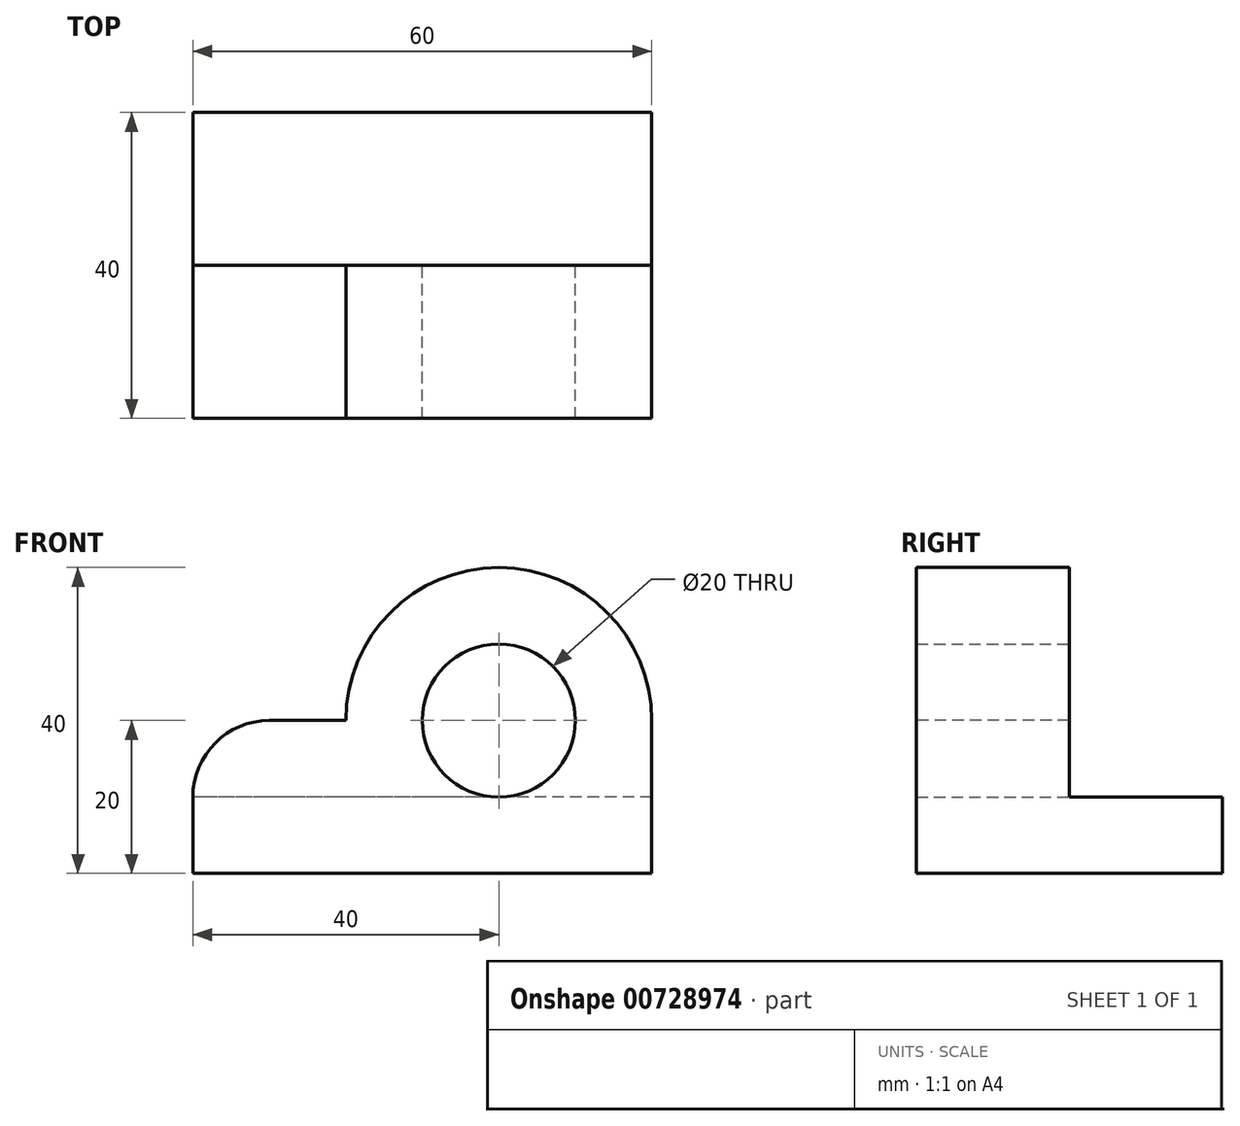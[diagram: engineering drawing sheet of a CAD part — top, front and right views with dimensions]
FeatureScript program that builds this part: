
annotation { "Feature Type Name" : "Feature", "Feature Type Description" : "" }
export const myFeature = defineFeature(function(context is Context, id is Id, definition is map)
    precondition{}
    {
        {
            var Q0;
            Q0=qCreatedBy(makeId("Top.planeOp"),FACE);
            var sketch = newSketch(context, id + "F0", { "sketchPlane" : qUnion([Q0])});
            skLineSegment(sketch, "E0.bottom", {"start": v(30, 20) * mm, "end": v(-30, 20) * mm});
            skLineSegment(sketch, "E0.top", {"start": v(30, -20) * mm, "end": v(-30, -20) * mm});
            skLineSegment(sketch, "E0.left", {"start": v(30, 20) * mm, "end": v(30, -20) * mm});
            skLineSegment(sketch, "E0.right", {"start": v(-30, 20) * mm, "end": v(-30, -20) * mm});
            skPoint(sketch, "E0.middle", {"position": v(0, 0) * mm});
            skSolve(sketch);
        }
        {
            var Q0;
            Q0=makeQuery(id+"F0.imprint","IMPRINT",FACE,{"disambiguationData":[TD([[makeQuery(id+"F0.imprint","IMPRINT",EDGE,{"derivedFrom":sQuery(id+"F0.wireOp",EDGE,"E0.bottom")}),1.0]])]});
            extrude(context, id + "F1", {"entities" : qUnion([Q0]), "depth" : 10 * mm, "offsetDistance" : 25 * mm});
        }
        {
            var Q0;
            Q0=makeQuery(id+"F1.opExtrude","CAP_FACE",FACE,{"disambiguationData":[OSD([sQuery(id+"F0.wireOp",EDGE,"E0.bottom"),sQuery(id+"F0.wireOp",EDGE,"E0.top"),sQuery(id+"F0.wireOp",EDGE,"E0.left"),sQuery(id+"F0.wireOp",EDGE,"E0.right")])],"isStart":false});
            var sketch = newSketch(context, id + "F2", { "sketchPlane" : qUnion([Q0])});
            skLineSegment(sketch, "E1.bottom", {"start": v(30, -20) * mm, "end": v(-30, -20) * mm});
            skLineSegment(sketch, "E1.top", {"start": v(30, 0) * mm, "end": v(-30, 0) * mm});
            skLineSegment(sketch, "E1.left", {"start": v(30, -20) * mm, "end": v(30, 0) * mm});
            skLineSegment(sketch, "E1.right", {"start": v(-30, -20) * mm, "end": v(-30, 0) * mm});
            skSolve(sketch);
        }
        {
            var Q0;
            Q0=makeQuery(id+"F2.imprint","IMPRINT",FACE,{"disambiguationData":[TD([[makeQuery(id+"F2.imprint","IMPRINT",EDGE,{"derivedFrom":sQuery(id+"F2.wireOp",EDGE,"E1.bottom")}),-1.0]])]});
            extrude(context, id + "F3", {"entities" : qUnion([Q0]), "operationType" : NewBodyOperationType.ADD, "depth" : 10 * mm, "offsetDistance" : 25 * mm});
        }
        {
            var Q0;
            Q0=makeQuery(id+"F3.opExtrude","SWEPT_FACE",FACE,{"disambiguationData":[OSD([sQuery(id+"F2.wireOp",EDGE,"E1.top")])]});
            var sketch = newSketch(context, id + "F4", { "sketchPlane" : qUnion([Q0])});
            skArc(sketch, "E2", {"start": v(10, 20) * mm, "mid": v(-10, 40) * mm, "end": v(-30, 20) * mm});
            skSolve(sketch);
        }
        {
            var Q0;
            {var subQ0=sQuery(id+"F4.wireOp",EDGE,"E2");Q0=makeQuery(id+"F4.imprint","IMPRINT",FACE,{"disambiguationData":[TD([[makeQuery(id+"F4.imprint","IMPRINT",EDGE,{"derivedFrom":subQ0}),1.0]])]});}
            extrude(context, id + "F5", {"entities" : qUnion([Q0]), "operationType" : NewBodyOperationType.ADD, "oppositeDirection" : true, "depth" : 20 * mm, "offsetDistance" : 25 * mm});
        }
        {
            var Q0;
            Q0=makeQuery(id+"F3.opExtrude","CAP_EDGE",EDGE,{"disambiguationData":[OSD([sQuery(id+"F2.wireOp",EDGE,"E1.right")])],"isStart":false});
            fillet(context, id + "F6", {"entities" : qUnion([Q0]), "radius" : 10 * mm, "tangentPropagation" : true, "allowEdgeOverflow" : false});
        }
        {
            var Q0;
            {var subQ0=sQuery(id+"F2.wireOp",EDGE,"E1.top");Q0=makeQuery(id+"F5.boolean.opBoolean","MERGE",FACE,{"derivedFrom":[makeQuery(id+"F3.opExtrude","SWEPT_FACE",FACE,{"disambiguationData":[OSD([subQ0])]}),makeQuery(id+"F5.opExtrude","CAP_FACE",FACE,{"disambiguationData":[OSD([subQ0,sQuery(id+"F4.wireOp",EDGE,"E2")])],"isStart":true})]});}
            var sketch = newSketch(context, id + "F7", { "sketchPlane" : qUnion([Q0])});
            skCircle(sketch, "E3", {"center": v(-10, 20) * mm, "radius": 10 * mm});
            skPoint(sketch, "E3.first.point", {"position": v(-10, 10) * mm});
            skPoint(sketch, "E3.second.point", {"position": v(-10.86, 29.96) * mm});
            skPoint(sketch, "E3.third.point", {"position": v(0, 20) * mm});
            skSolve(sketch);
        }
        {
            var Q0;
            Q0=makeQuery(id+"F7.imprint","IMPRINT",FACE,{"disambiguationData":[TD([[makeQuery(id+"F7.imprint","IMPRINT",EDGE,{"derivedFrom":sQuery(id+"F7.wireOp",EDGE,"E3")}),1.0]])]});
            extrude(context, id + "F8", {"entities" : qUnion([Q0]), "operationType" : NewBodyOperationType.REMOVE, "oppositeDirection" : true, "depth" : 20 * mm, "offsetDistance" : 25 * mm});
        }
    });
